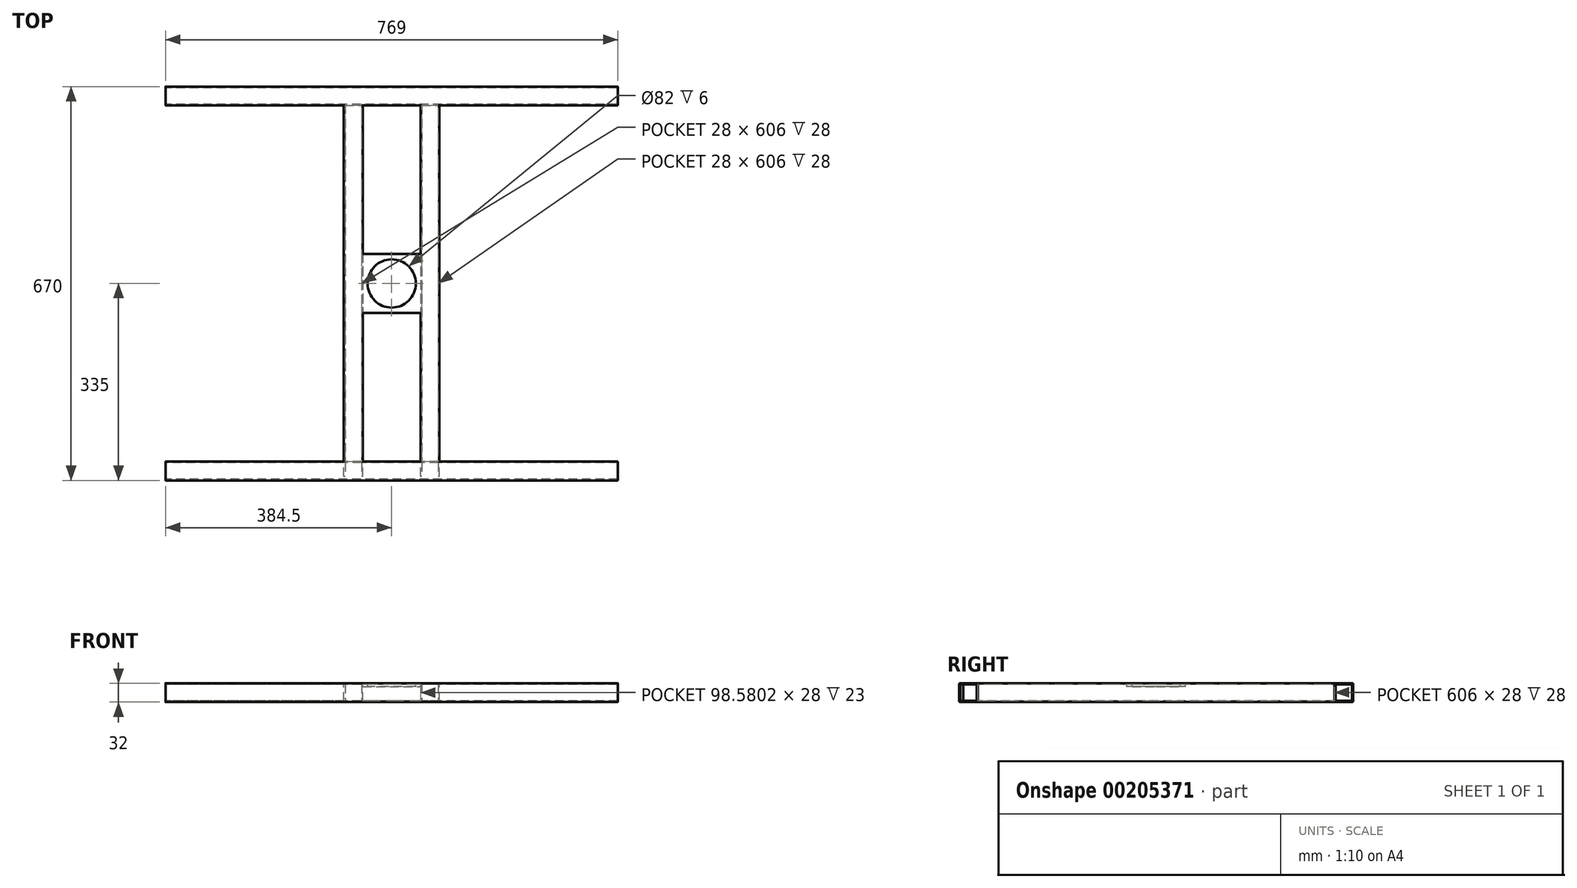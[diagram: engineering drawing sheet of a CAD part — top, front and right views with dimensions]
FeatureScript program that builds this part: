
annotation { "Feature Type Name" : "Feature", "Feature Type Description" : "" }
export const myFeature = defineFeature(function(context is Context, id is Id, definition is map)
    precondition{}
    {
        {
            var Q0;
            Q0=qCreatedBy(makeId("Right.planeOp"),FACE);
            var sketch = newSketch(context, id + "F0", { "sketchPlane" : qUnion([Q0])});
            skLineSegment(sketch, "E0.bottom", {"start": v(-333, -16) * mm, "end": v(-305, -16) * mm});
            skLineSegment(sketch, "E0.top", {"start": v(-333, 16) * mm, "end": v(-305, 16) * mm});
            skLineSegment(sketch, "E0.left", {"start": v(-335, -14) * mm, "end": v(-335, 14) * mm});
            skLineSegment(sketch, "E0.right", {"start": v(-303, -14) * mm, "end": v(-303, 14) * mm});
            skPoint(sketch, "E0.middle", {"position": v(-319, 0) * mm});
            skLineSegment(sketch, "E1.bottom", {"start": v(-333, 14) * mm, "end": v(-305, 14) * mm});
            skLineSegment(sketch, "E1.top", {"start": v(-333, -14) * mm, "end": v(-305, -14) * mm});
            skLineSegment(sketch, "E1.left", {"start": v(-333, 14) * mm, "end": v(-333, -14) * mm});
            skLineSegment(sketch, "E1.right", {"start": v(-305, 14) * mm, "end": v(-305, -14) * mm});
            skPoint(sketch, "E2.visualSharp", {"position": v(-335, 16) * mm});
            skArc(sketch, "E2.filletArc", {"start": v(-333, 16) * mm, "mid": v(-334.41, 15.41) * mm, "end": v(-335, 14) * mm});
            skPoint(sketch, "E3.visualSharp", {"position": v(-335, -16) * mm});
            skArc(sketch, "E3.filletArc", {"start": v(-335, -14) * mm, "mid": v(-334.41, -15.41) * mm, "end": v(-333, -16) * mm});
            skPoint(sketch, "E4.visualSharp", {"position": v(-303, -16) * mm});
            skArc(sketch, "E4.filletArc", {"start": v(-305, -16) * mm, "mid": v(-303.59, -15.41) * mm, "end": v(-303, -14) * mm});
            skPoint(sketch, "E5.visualSharp", {"position": v(-303, 16) * mm});
            skArc(sketch, "E5.filletArc", {"start": v(-303, 14) * mm, "mid": v(-303.59, 15.41) * mm, "end": v(-305, 16) * mm});
            skLineSegment(sketch, "E6", {"start": v(-319, 0) * mm, "end": v(0, 0) * mm, "construction": true});
            skArc(sketch, "E7.MirrorCS", {"start": v(333, 16) * mm, "mid": v(334.41, 15.41) * mm, "end": v(335, 14) * mm});
            skArc(sketch, "E8.MirrorCS", {"start": v(335, -14) * mm, "mid": v(334.41, -15.41) * mm, "end": v(333, -16) * mm});
            skArc(sketch, "E9.MirrorCS", {"start": v(303, 14) * mm, "mid": v(303.59, 15.41) * mm, "end": v(305, 16) * mm});
            skArc(sketch, "E10.MirrorCS", {"start": v(305, -16) * mm, "mid": v(303.59, -15.41) * mm, "end": v(303, -14) * mm});
            skPoint(sketch, "E11.MirrorP", {"position": v(319, 0) * mm});
            skLineSegment(sketch, "E12.MirrorCS", {"start": v(305, 14) * mm, "end": v(305, -14) * mm});
            skPoint(sketch, "E13.MirrorP", {"position": v(335, -16) * mm});
            skLineSegment(sketch, "E14.MirrorCS", {"start": v(333, 14) * mm, "end": v(333, -14) * mm});
            skLineSegment(sketch, "E15.MirrorCS", {"start": v(319, 0) * mm, "end": v(0, 0) * mm, "construction": true});
            skPoint(sketch, "E16.MirrorP", {"position": v(335, 16) * mm});
            skPoint(sketch, "E17.MirrorP", {"position": v(303, -16) * mm});
            skLineSegment(sketch, "E18.MirrorCS", {"start": v(333, -14) * mm, "end": v(305, -14) * mm});
            skLineSegment(sketch, "E19.MirrorCS", {"start": v(333, 14) * mm, "end": v(305, 14) * mm});
            skPoint(sketch, "E20.MirrorP", {"position": v(303, 16) * mm});
            skLineSegment(sketch, "E21.MirrorCS", {"start": v(303, -14) * mm, "end": v(303, 14) * mm});
            skLineSegment(sketch, "E22.MirrorCS", {"start": v(335, -14) * mm, "end": v(335, 14) * mm});
            skLineSegment(sketch, "E23.MirrorCS", {"start": v(333, 16) * mm, "end": v(305, 16) * mm});
            skLineSegment(sketch, "E24.MirrorCS", {"start": v(333, -16) * mm, "end": v(305, -16) * mm});
            skSolve(sketch);
        }
        {
            var Q0;
            Q0 = qSketchRegion(id + "F0", true);
            extrude(context, id + "F1", {"entities" : qUnion([Q0]), "endBound" : BoundingType.SYMMETRIC, "depth" : 769 * mm});
        }
        {
            var Q0;
            Q0=makeQuery(id+"F1.opExtrude","SWEPT_FACE",FACE,{"disambiguationData":[OSD([sQuery(id+"F0.wireOp",EDGE,"E0.right")])]});
            var sketch = newSketch(context, id + "F2", { "sketchPlane" : qUnion([Q0])});
            skLineSegment(sketch, "E25", {"start": v(0, 14) * mm, "end": v(0, -14) * mm, "construction": true});
            skLineSegment(sketch, "E26", {"start": v(0, -14) * mm, "end": v(0, -6.92) * mm});
            skLineSegment(sketch, "E27", {"start": v(0, 0) * mm, "end": v(-65.3, 0) * mm, "construction": true});
            skPoint(sketch, "E27.endSnap0", {"position": v(0, 0) * mm});
            skLineSegment(sketch, "E28.bottom", {"start": v(-81.3, -16) * mm, "end": v(-49.3, -16) * mm});
            skLineSegment(sketch, "E28.top", {"start": v(-81.3, 16) * mm, "end": v(-49.3, 16) * mm});
            skLineSegment(sketch, "E28.left", {"start": v(-81.3, -16) * mm, "end": v(-81.3, 16) * mm});
            skLineSegment(sketch, "E28.right", {"start": v(-49.3, -16) * mm, "end": v(-49.3, 16) * mm});
            skPoint(sketch, "E28.middle", {"position": v(-65.3, 0) * mm});
            skLineSegment(sketch, "E29.0", {"start": v(-79.3, -14) * mm, "end": v(-79.3, 14) * mm});
            skLineSegment(sketch, "E29.1", {"start": v(-79.3, -14) * mm, "end": v(-51.3, -14) * mm});
            skLineSegment(sketch, "E29.2", {"start": v(-51.3, -14) * mm, "end": v(-51.3, 14) * mm});
            skLineSegment(sketch, "E29.3", {"start": v(-79.3, 14) * mm, "end": v(-51.3, 14) * mm});
            skLineSegment(sketch, "E30.MirrorCS", {"start": v(81.3, -16) * mm, "end": v(81.3, 16) * mm});
            skLineSegment(sketch, "E31.MirrorCS", {"start": v(81.3, 16) * mm, "end": v(49.3, 16) * mm});
            skLineSegment(sketch, "E32.MirrorCS", {"start": v(49.3, -16) * mm, "end": v(49.3, 16) * mm});
            skLineSegment(sketch, "E33.MirrorCS", {"start": v(81.3, -16) * mm, "end": v(49.3, -16) * mm});
            skLineSegment(sketch, "E34.MirrorCS", {"start": v(79.3, -14) * mm, "end": v(51.3, -14) * mm});
            skLineSegment(sketch, "E35.MirrorCS", {"start": v(79.3, -14) * mm, "end": v(79.3, 14) * mm});
            skLineSegment(sketch, "E36.MirrorCS", {"start": v(79.3, 14) * mm, "end": v(51.3, 14) * mm});
            skLineSegment(sketch, "E37.MirrorCS", {"start": v(51.3, -14) * mm, "end": v(51.3, 14) * mm});
            skLineSegment(sketch, "E38.bottom", {"start": v(51.15, 62.93) * mm, "end": v(-51.15, 62.93) * mm, "construction": true});
            skLineSegment(sketch, "E38.top", {"start": v(51.15, -62.93) * mm, "end": v(-51.15, -62.93) * mm, "construction": true});
            skLineSegment(sketch, "E38.left", {"start": v(51.15, 62.93) * mm, "end": v(51.15, -62.93) * mm, "construction": true});
            skLineSegment(sketch, "E38.right", {"start": v(-51.15, 62.93) * mm, "end": v(-51.15, -62.93) * mm, "construction": true});
            skSolve(sketch);
        }
        {
            var Q0;
            Q0 = qSketchRegion(id + "F2", true);
            var Q1;
            Q1 = qSketchRegion(id + "F2", true);
            extrude(context, id + "F3", {"entities" : qUnion([Q0, Q1]), "operationType" : NewBodyOperationType.ADD, "endBound" : BoundingType.UP_TO_NEXT, "depth" : 25 * mm, "hasSecondDirection" : true, "secondDirectionOppositeDirection" : true, "secondDirectionDepth" : 25 * mm});
        }
        {
            var Q0;
            Q0=makeQuery(id+"FsL87WSfcs1dLFI_2.boolean.opBoolean","MERGE",FACE,{"derivedFrom":[makeQuery(id+"F1.opExtrude","SWEPT_FACE",FACE,{"disambiguationData":[OSD([sQuery(id+"F0.wireOp",EDGE,"E23.MirrorCS")])]}),makeQuery(id+"FsL87WSfcs1dLFI_2.opExtrude","SWEPT_FACE",FACE,{"disambiguationData":[OSD([sQuery(id+"F2.wireOp",EDGE,"E28.top")])]}),makeQuery(id+"FsL87WSfcs1dLFI_2.opExtrude","SWEPT_FACE",FACE,{"disambiguationData":[OSD([sQuery(id+"F2.wireOp",EDGE,"E31.MirrorCS")])]})]});
            var sketch = newSketch(context, id + "F4", { "sketchPlane" : qUnion([Q0])});
            skPoint(sketch, "E39.middle", {"position": v(0, 0) * mm});
            skPoint(sketch, "E39.left.end.orphan", {"position": v(-50.7, 49.3) * mm});
            skPoint(sketch, "E39.bottom.start.orphan", {"position": v(-49.3, -50.7) * mm});
            skPoint(sketch, "E39.right.end.orphan", {"position": v(49.3, 50.7) * mm});
            skPoint(sketch, "E39.right.start.orphan", {"position": v(50.7, -49.3) * mm});
            skLineSegment(sketch, "E40.bottom", {"start": v(-50, -50) * mm, "end": v(50, -50) * mm});
            skLineSegment(sketch, "E40.top", {"start": v(-50, 50) * mm, "end": v(50, 50) * mm});
            skLineSegment(sketch, "E40.left", {"start": v(-50, -50) * mm, "end": v(-50, 50) * mm});
            skLineSegment(sketch, "E40.right", {"start": v(50, -50) * mm, "end": v(50, 50) * mm});
            skSolve(sketch);
        }
        {
            var Q0;
            {var subQ0=sQuery(id+"F4.wireOp",EDGE,"E40.bottom");var subQ1=makeQuery(id+"F3.opExtrude","SWEPT_EDGE",EDGE,{"disambiguationData":[OSD([sQuery(id+"F2.wireOp",EDGE,"E31.MirrorCS"),sQuery(id+"F2.wireOp",EDGE,"E32.MirrorCS")])]});var subQ2=makeQuery(id+"F4.imprint","INTERSECT",VERTEX,{"derivedFrom":[subQ1,subQ0]});Q0=makeQuery(id+"F4.imprint","IMPRINT",FACE,{"disambiguationData":[TD([[makeQuery(id+"F4.imprint","IMPRINT",EDGE,{"disambiguationData":[TD([[subQ2,-1.0]])],"derivedFrom":subQ0}),1.0]])]});}
            var Q1;
            {var subQ0=sQuery(id+"F4.wireOp",EDGE,"E40.bottom");var subQ1=makeQuery(id+"F3.opExtrude","SWEPT_EDGE",EDGE,{"disambiguationData":[OSD([sQuery(id+"F2.wireOp",EDGE,"E31.MirrorCS"),sQuery(id+"F2.wireOp",EDGE,"E32.MirrorCS")])]});var subQ2=makeQuery(id+"F4.imprint","INTERSECT",VERTEX,{"derivedFrom":[subQ1,subQ0]});Q1=makeQuery(id+"F4.imprint","IMPRINT",FACE,{"disambiguationData":[TD([[makeQuery(id+"F4.imprint","IMPRINT",EDGE,{"disambiguationData":[TD([[subQ2,-1.0]])],"derivedFrom":subQ0}),1.0]])]});}
            extrude(context, id + "F5", {"entities" : qUnion([Q0, Q1]), "operationType" : NewBodyOperationType.ADD, "oppositeDirection" : true, "depth" : 6 * mm});
        }
        {
            var Q0;
            Q0=makeQuery(id+"F5.boolean.opBoolean","MERGE",FACE,{"derivedFrom":[makeQuery(id+"FsL87WSfcs1dLFI_2.boolean.opBoolean","MERGE",FACE,{"derivedFrom":[makeQuery(id+"F1.opExtrude","SWEPT_FACE",FACE,{"disambiguationData":[OSD([sQuery(id+"F0.wireOp",EDGE,"E23.MirrorCS")])]}),makeQuery(id+"FsL87WSfcs1dLFI_2.opExtrude","SWEPT_FACE",FACE,{"disambiguationData":[OSD([sQuery(id+"F2.wireOp",EDGE,"E28.top")])]}),makeQuery(id+"FsL87WSfcs1dLFI_2.opExtrude","SWEPT_FACE",FACE,{"disambiguationData":[OSD([sQuery(id+"F2.wireOp",EDGE,"E31.MirrorCS")])]})]}),makeQuery(id+"F5.opExtrude","CAP_FACE",FACE,{"disambiguationData":[OSD([sQuery(id+"F4.wireOp",EDGE,"E40.bottom"),sQuery(id+"F4.wireOp",EDGE,"E40.top"),sQuery(id+"F4.wireOp",EDGE,"E40.left"),sQuery(id+"F4.wireOp",EDGE,"E40.right")])],"isStart":true})]});
            var sketch = newSketch(context, id + "F6", { "sketchPlane" : qUnion([Q0])});
            skCircle(sketch, "E41", {"center": v(0, 0) * mm, "radius": 41 * mm});
            skSolve(sketch);
        }
        {
            var Q0;
            Q0 = qSketchRegion(id + "F6", true);
            extrude(context, id + "F7", {"entities" : qUnion([Q0]), "operationType" : NewBodyOperationType.REMOVE, "endBound" : BoundingType.THROUGH_ALL, "oppositeDirection" : true, "depth" : 25 * mm});
        }
    });
